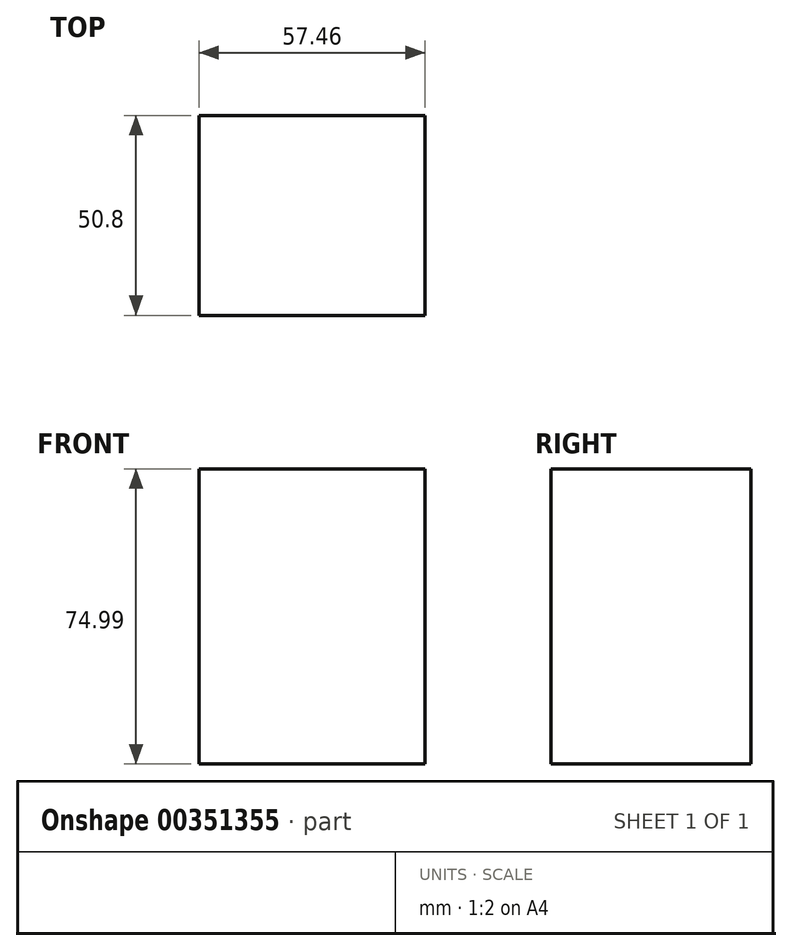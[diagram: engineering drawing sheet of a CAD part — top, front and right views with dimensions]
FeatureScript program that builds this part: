
annotation { "Feature Type Name" : "Feature", "Feature Type Description" : "" }
export const myFeature = defineFeature(function(context is Context, id is Id, definition is map)
    precondition{}
    {
        {
            var Q0;
            Q0=qCreatedBy(makeId("Front.planeOp"),FACE);
            var sketch = newSketch(context, id + "F0", { "sketchPlane" : qUnion([Q0])});
            skLineSegment(sketch, "E0.bottom", {"start": v(-23.7, 22.08) * mm, "end": v(33.76, 22.08) * mm});
            skLineSegment(sketch, "E0.top", {"start": v(-23.7, -52.91) * mm, "end": v(33.76, -52.91) * mm});
            skLineSegment(sketch, "E0.left", {"start": v(-23.7, 22.08) * mm, "end": v(-23.7, -52.91) * mm});
            skLineSegment(sketch, "E0.right", {"start": v(33.76, 22.08) * mm, "end": v(33.76, -52.91) * mm});
            skSolve(sketch);
        }
        {
            var Q0;
            Q0 = qSketchRegion(id + "F0", true);
            extrude(context, id + "F1", {"entities" : qUnion([Q0]), "depth" : 50.8 * mm});
        }
    });
